# Revit family: PRD_AR_ShwrMxrs_BasicInstallationKitForShower_F5BX2001
name_source: partatom
category: Plumbing Fixtures
revit_build: Autodesk Revit 2018 (Build: 20190510_1515(x64)
units: mm (PartAtom-declared; Revit-internal decimal feet)

## family parameters
Cut with Voids When Loaded = Yes
Host = Face
OmniClass Number = 23.45.05.14.99
OmniClass Title = Other Sanitary Washing Plumbing Fixtures
Part Type = Normal
Room Calculation Point = No
Round Connector Dimension = Use Diameter
Shared = No

## types (1)
- F5BX2001
    Application = shower-taps
    AssetType = Fixed
    BIMObjectName = PRD_AR_ShowerMixers_BasicInstallationKitForShower_F5BX2001
    BarrierFree = no
    Category = Pr_40_20_87_78, Shower manual water supply sets
    CloseOffRating = 0.0 Pa
    Default Elevation = 850 mm  [stored 2.78871 ft]
    Description = R5 basic installation kit with sliding adhesive flange for in-wall mounting of finished installation kits DN 15 with mixing unit, for shower facilities. For connection to hot and cold water. KWC system box made of plastic, 174 x 225 mm, with lockable connection screws, shell protection, flush connector for flushing and leak test. Continuously-adjustable sliding adhesive flange with form-closed, flexible, 70 mm wide sealing collar. Sealing collar made of water-tight, permanently-elastic, alkali-resistant, and crack-bridging thermoplastic elastomer with polypropylene fleece for connecting to compound seals in dry and wet construction.
    DiameterNominal = 15.000 mm
    DurationUnit = year
    Features = For connection to hot and cold water, 174 x 225 mm.
    Finish = synthetic
    FlowCoefficient = 0
    FlowColdWater = 0.0 L/s
    FlowHotWater = 0.0 L/s
    GrossWeight = 1.45 kg
    IfcExportAs = IfcValveType
    IfcExportType = MIXING
    Manufacturer = KWC Group AG
    ManufacturerName = KWC Group AG
    ManufacturerURL = www.kwc.com
    Material = Plastic
    MaterialsBody = Brass
    MixerControl = Other
    Model = F5BX2001
    ModelNumber = 2030028990
    ModelReference = F5BX2001
    NBSDescription = Shower manual water supply sets
    NBSReference = 45-35-70/335
    Name = F5 basic installation kit for shower F5BX2001
    NetWeight = 1.36 kg
    NominalHeight = 0 mm  [stored 0 ft]
    NominalLength = 0 mm  [stored 0 ft]
    NominalWidth = 0 mm  [stored 0 ft]
    OutletConnectionSize = 15 mm  [stored 0.0492126 ft]
    OutletSize = G-1-2-B
    PositionOfPowerConnection = from top
    ProductInformation = https://pim.kwc.com
    Size = DN 15
    TestPressure = 0.0 Pa
    Type = for built-in with box and adhesive flange
    TypeOfMixing = with thermostat / mixer
    TypeOfMounting = in-wall installation with box
    URL = www.kwc.com
    Uniclass2015Code = Pr_40_20_87_78
    Uniclass2015Title = Shower manual water supply sets
    Uniclass2015Version = Products v1.10
    ValveMaterial = PRD_AR_PlasticRed
    ValveMechanism = Other
    ValveOperation = Other
    ValvePattern = ANGLED_2_PORT
    Version = 1
    WarrantyDurationUnit = year

note: [stored X ft] marks values corroborated as IEEE doubles in the binary element streams (Revit-internal decimal feet)

## geometry (parser evidence)
native form markers: Sweep x2
no freeform markers — native parametric forms only
